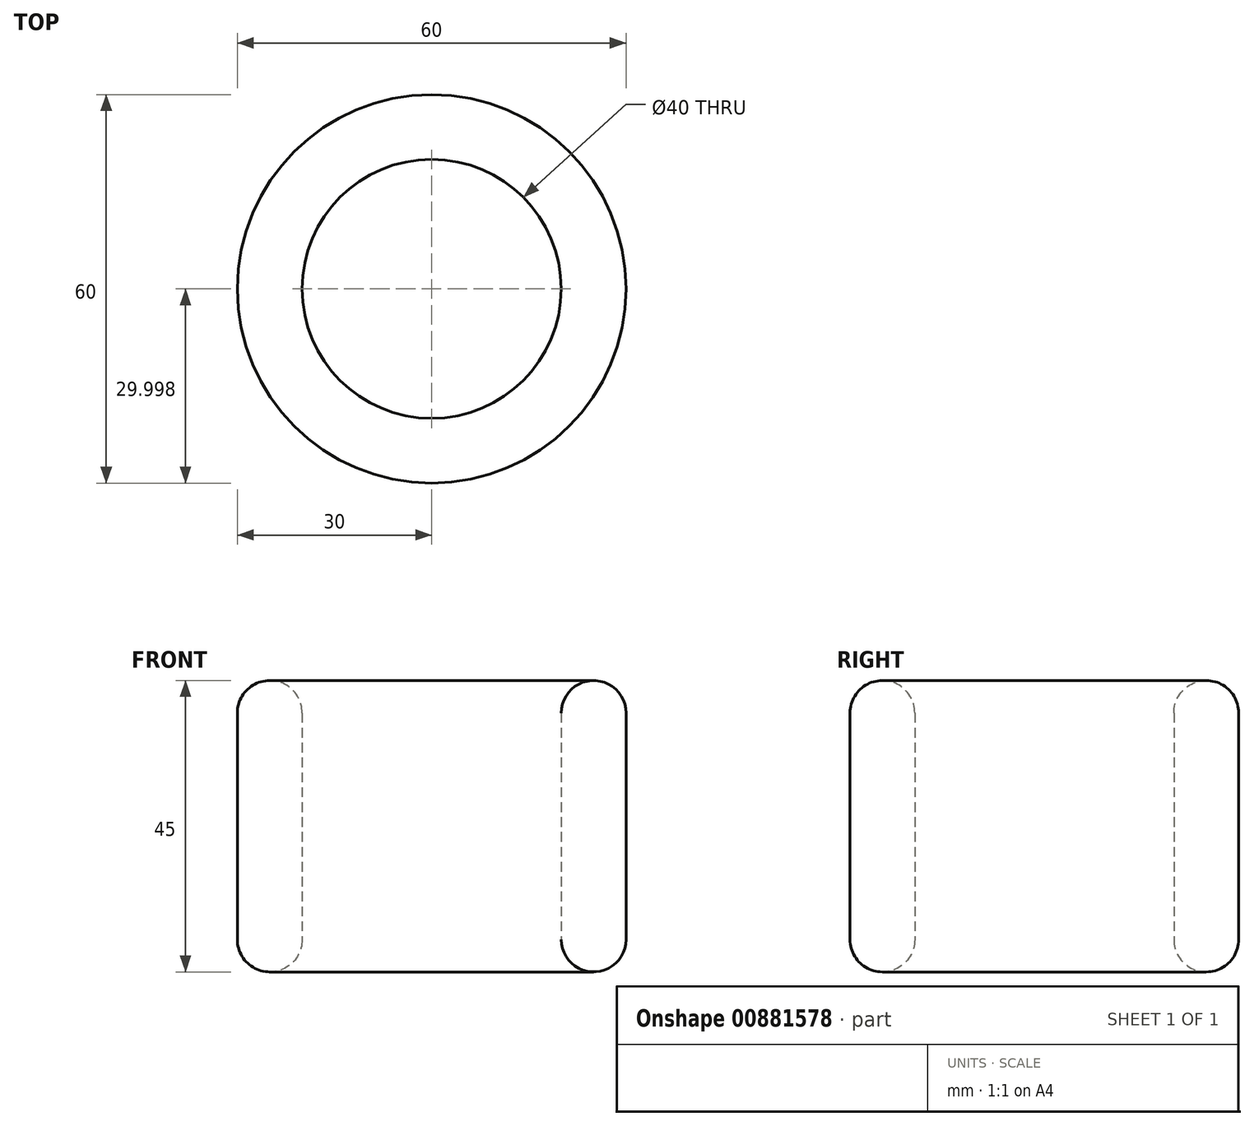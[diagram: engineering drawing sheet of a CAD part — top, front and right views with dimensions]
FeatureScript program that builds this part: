
annotation { "Feature Type Name" : "Feature", "Feature Type Description" : "" }
export const myFeature = defineFeature(function(context is Context, id is Id, definition is map)
    precondition{}
    {
        {
            var Q0;
            Q0=qCreatedBy(makeId("Top.planeOp"),FACE);
            var sketch = newSketch(context, id + "F0", { "sketchPlane" : qUnion([Q0])});
            skCircle(sketch, "E0", {"center": v(0, -1.93) * mm, "radius": 30 * mm});
            skCircle(sketch, "E1.0", {"center": v(0, -1.93) * mm, "radius": 20 * mm});
            skSolve(sketch);
        }
        {
            var Q0;
            Q0 = qSketchRegion(id + "F0", true);
            extrude(context, id + "F1", {"entities" : qUnion([Q0]), "depth" : 45 * mm, "offsetDistance" : 25 * mm});
        }
        {
            var Q0;
            Q0=makeQuery(id+"F1.opExtrude","CAP_EDGE",EDGE,{"disambiguationData":[OSD([sQuery(id+"F0.wireOp",EDGE,"E0")])],"isStart":true});
            var Q1;
            Q1=makeQuery(id+"F1.opExtrude","CAP_EDGE",EDGE,{"disambiguationData":[OSD([sQuery(id+"F0.wireOp",EDGE,"E1.0")])],"isStart":true});
            var Q2;
            Q2=makeQuery(id+"F1.opExtrude","CAP_EDGE",EDGE,{"disambiguationData":[OSD([sQuery(id+"F0.wireOp",EDGE,"E1.0")])],"isStart":false});
            var Q3;
            Q3=makeQuery(id+"F1.opExtrude","CAP_EDGE",EDGE,{"disambiguationData":[OSD([sQuery(id+"F0.wireOp",EDGE,"E0")])],"isStart":false});
            fillet(context, id + "F2", {"entities" : qUnion([Q0, Q1, Q2, Q3]), "radius" : 5 * mm, "tangentPropagation" : true, "allowEdgeOverflow" : false});
        }
    });
